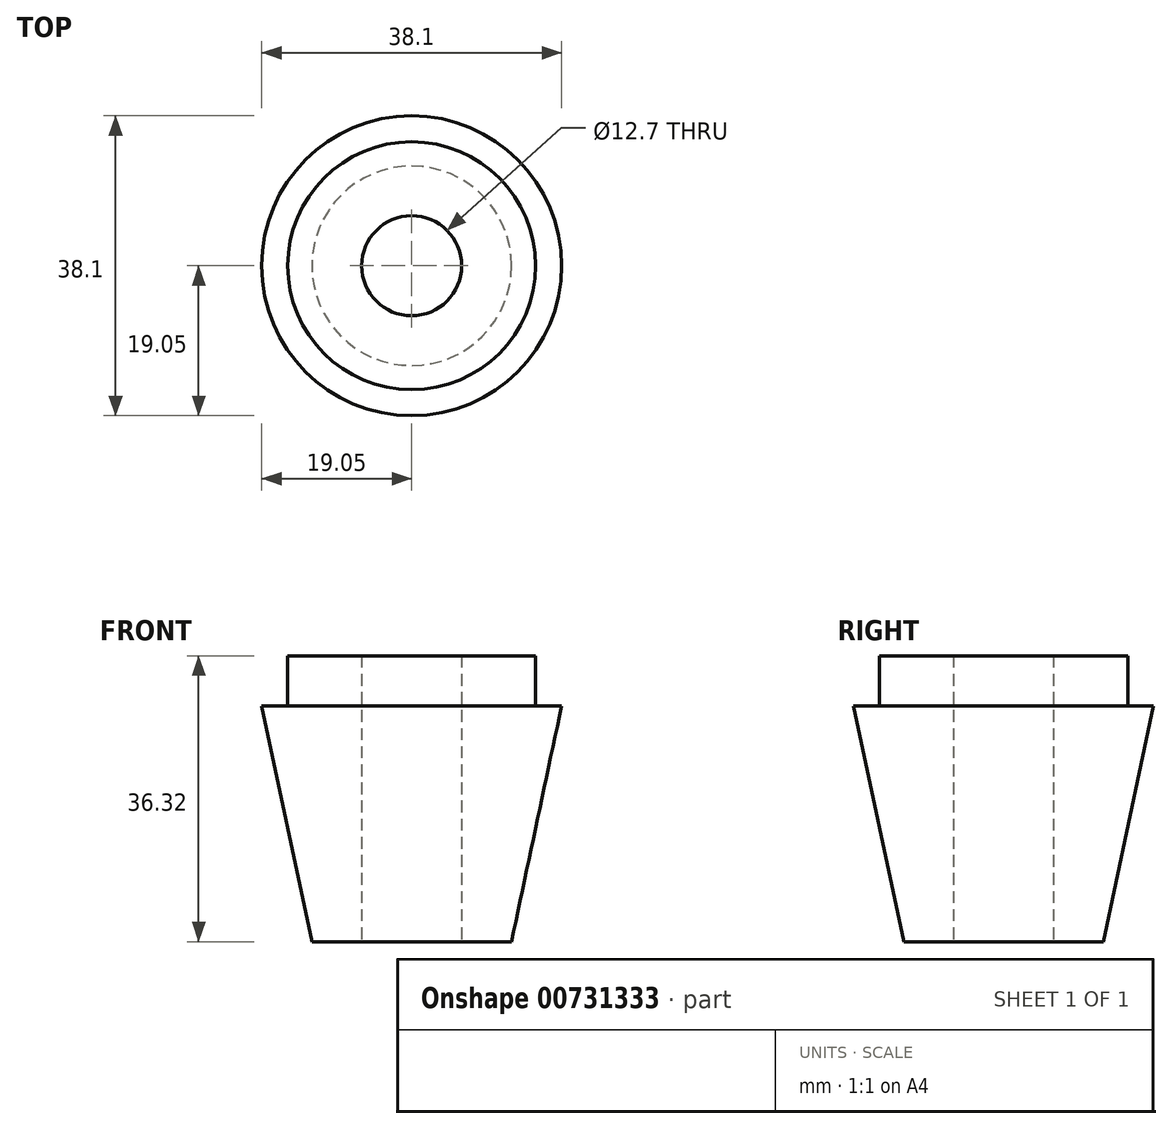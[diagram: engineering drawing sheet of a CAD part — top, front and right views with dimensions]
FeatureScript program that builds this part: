
annotation { "Feature Type Name" : "Feature", "Feature Type Description" : "" }
export const myFeature = defineFeature(function(context is Context, id is Id, definition is map)
    precondition{}
    {
        {
            var Q0;
            Q0=qCreatedBy(makeId("Top.planeOp"),FACE);
            var sketch = newSketch(context, id + "F0", { "sketchPlane" : qUnion([Q0])});
            skCircle(sketch, "E0", {"center": v(0, 0) * mm, "radius": 15.75 * mm});
            skCircle(sketch, "E1", {"center": v(0, 0) * mm, "radius": 19.19 * mm});
            skSolve(sketch);
        }
        {
            var Q0;
            Q0=makeQuery(id+"F0.imprint","IMPRINT",FACE,{"disambiguationData":[TD([[makeQuery(id+"F0.imprint","IMPRINT",EDGE,{"derivedFrom":sQuery(id+"F0.wireOp",EDGE,"E0")}),1.0]])]});
            extrude(context, id + "F1", {"entities" : qUnion([Q0]), "depth" : 6.35 * mm, "offsetDistance" : 25.4 * mm});
        }
        {
            var Q0;
            Q0=qCreatedBy(makeId("Top.planeOp"),FACE);
            var sketch = newSketch(context, id + "F2", { "sketchPlane" : qUnion([Q0])});
            skCircle(sketch, "E2", {"center": v(0, 0) * mm, "radius": 19.05 * mm});
            skSolve(sketch);
        }
        {
            var Q0;
            Q0=qCreatedBy(makeId("Top.planeOp"),FACE);
            cPlane(context, id + "F3", {"entities" : qUnion([Q0]), "cplaneType" : CPlaneType.OFFSET, "offset" : 29.97 * mm, "oppositeDirection" : true, "width" : 152.4 * mm, "height" : 152.4 * mm});
        }
        {
            var Q0;
            Q0 = qSketchRegion(id + "F2", true);
            extrude(context, id + "F4", {"entities" : qUnion([Q0]), "operationType" : NewBodyOperationType.ADD, "oppositeDirection" : true, "depth" : 29.97 * mm, "offsetDistance" : 25.4 * mm, "hasDraft" : true, "draftAngle" : 12 * degree, "draftPullDirection" : true});
        }
        {
            var Q0;
            Q0=qCreatedBy(id+"F3.planeOp",FACE);
            var sketch = newSketch(context, id + "F5", { "sketchPlane" : qUnion([Q0])});
            skPoint(sketch, "E3", {"position": v(0, 0) * mm});
            skSolve(sketch);
        }
        {
            var Q0;
            Q0=sQuery(id+"F5.wireOp",VERTEX,"E3");
            var Q1;
            Q1=makeQuery(id+"F1.opExtrude","SWEPT_BODY",BODY,{"disambiguationData":[OSD([sQuery(id+"F0.wireOp",EDGE,"E0")])]});
            hole(context, id + "F6", {"style" : HoleStyle.SIMPLE, "endStyle" : HoleEndStyle.THROUGH, "oppositeDirection" : true, "holeDiameter" : 12.7 * mm, "majorDiameter" : 6.35 * mm, "isTappedThrough" : true, "tappedDepth" : 12.7 * mm, "tapClearance" : 3, "locations" : qUnion([Q0]), "scope" : qUnion([Q1])});
        }
    });
